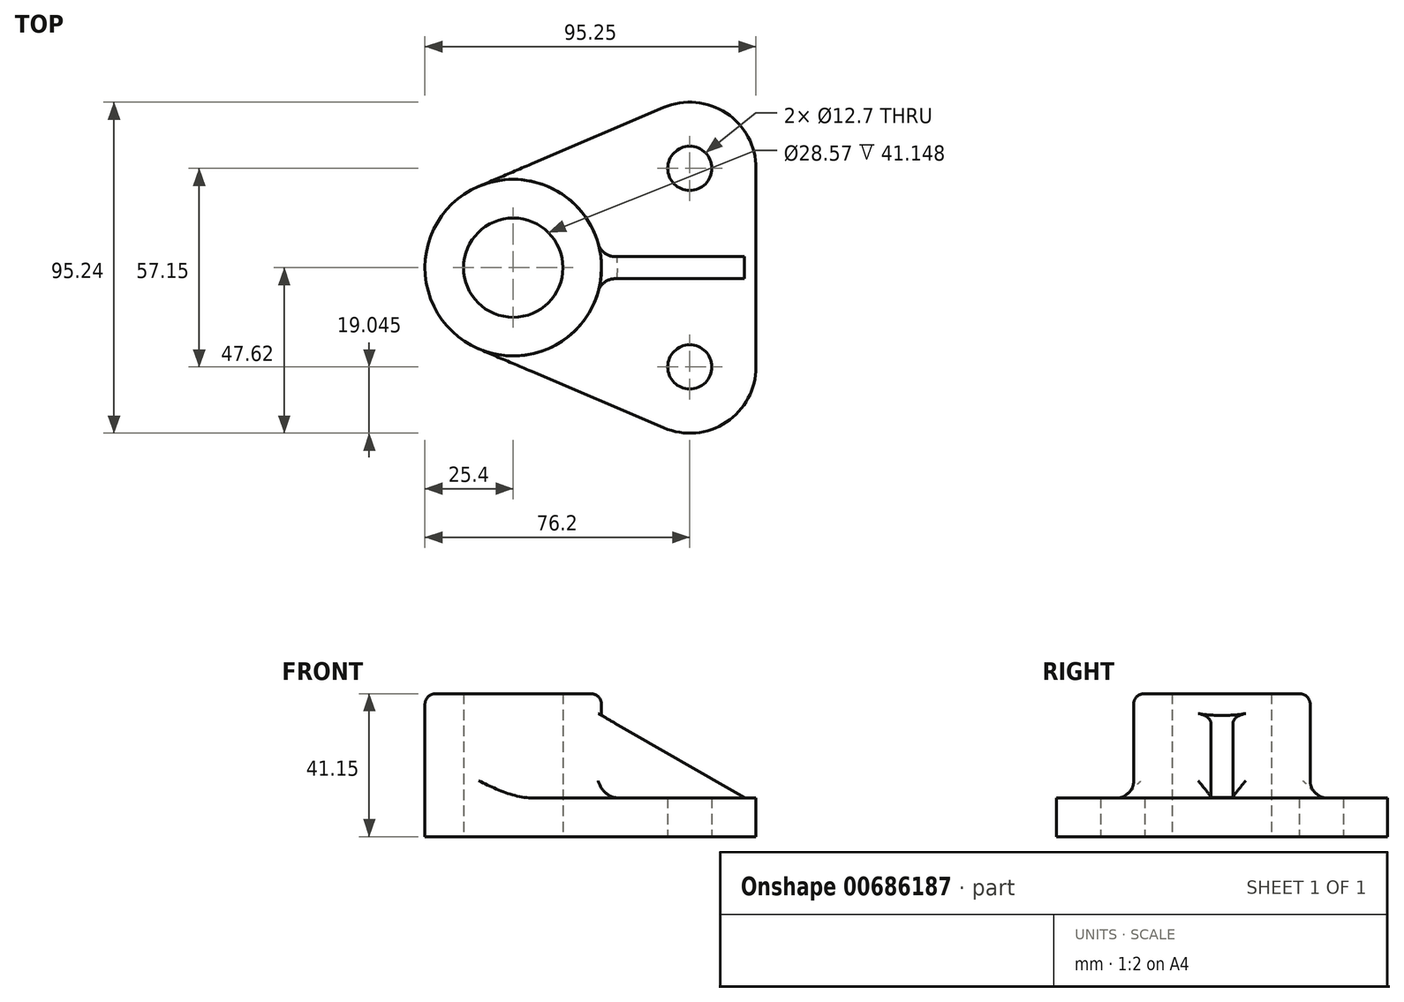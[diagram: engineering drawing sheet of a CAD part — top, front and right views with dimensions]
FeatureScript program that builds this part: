
annotation { "Feature Type Name" : "Feature", "Feature Type Description" : "" }
export const myFeature = defineFeature(function(context is Context, id is Id, definition is map)
    precondition{}
    {
        {
            var Q0;
            Q0=qCreatedBy(makeId("Top.planeOp"),FACE);
            var sketch = newSketch(context, id + "F0", { "sketchPlane" : qUnion([Q0])});
            skCircle(sketch, "E0", {"center": v(0, 0) * mm, "radius": 25.4 * mm});
            skCircle(sketch, "E1", {"center": v(0, 0) * mm, "radius": 14.29 * mm});
            skLineSegment(sketch, "E2", {"start": v(-34.33, 0) * mm, "end": v(50.8, 0) * mm, "construction": true});
            skCircle(sketch, "E3", {"center": v(50.8, 28.58) * mm, "radius": 6.35 * mm});
            skCircle(sketch, "E4", {"center": v(50.8, -28.58) * mm, "radius": 6.35 * mm});
            skArc(sketch, "E5", {"start": v(69.85, 28.58) * mm, "mid": v(61.3, 44.47) * mm, "end": v(43.33, 46.1) * mm});
            skArc(sketch, "E6", {"start": v(43.33, -46.1) * mm, "mid": v(61.3, -44.47) * mm, "end": v(69.85, -28.58) * mm});
            skLineSegment(sketch, "E7", {"start": v(-9.97, 23.36) * mm, "end": v(43.33, 46.1) * mm});
            skLineSegment(sketch, "E8", {"start": v(-9.97, -23.36) * mm, "end": v(43.33, -46.1) * mm});
            skLineSegment(sketch, "E9", {"start": v(69.85, 28.58) * mm, "end": v(69.85, -28.58) * mm});
            skPoint(sketch, "E10.right.end.orphan", {"position": v(-66.55, 3.17) * mm});
            skPoint(sketch, "E11.orphan", {"position": v(-66.55, -3.18) * mm});
            skPoint(sketch, "E10.left.end.orphan", {"position": v(66.55, 3.18) * mm});
            skPoint(sketch, "E10.left.start.orphan", {"position": v(66.55, -3.18) * mm});
            skSolve(sketch);
        }
        {
            var Q0;
            Q0=makeQuery(id+"F0.imprint","IMPRINT",FACE,{"disambiguationData":[TD([[makeQuery(id+"F0.imprint","IMPRINT",EDGE,{"derivedFrom":sQuery(id+"F0.wireOp",EDGE,"E1")}),-1.0]])]});
            extrude(context, id + "F1", {"entities" : qUnion([Q0]), "depth" : 41.15 * mm, "offsetDistance" : 25.4 * mm});
        }
        {
            var Q0;
            Q0=makeQuery(id+"F0.imprint","IMPRINT",FACE,{"disambiguationData":[TD([[makeQuery(id+"F0.imprint","IMPRINT",EDGE,{"derivedFrom":sQuery(id+"F0.wireOp",EDGE,"E3")}),-1.0]])]});
            extrude(context, id + "F2", {"entities" : qUnion([Q0]), "operationType" : NewBodyOperationType.ADD, "depth" : 11.18 * mm, "offsetDistance" : 25.4 * mm});
        }
        {
            var Q0;
            Q0=qCreatedBy(makeId("Front.planeOp"),FACE);
            var sketch = newSketch(context, id + "F3", { "sketchPlane" : qUnion([Q0])});
            skLineSegment(sketch, "E12", {"start": v(25.4, 11.18) * mm, "end": v(66.55, 11.25) * mm});
            skLineSegment(sketch, "E13", {"start": v(66.55, 11.25) * mm, "end": v(22.94, 36.32) * mm});
            skLineSegment(sketch, "E14.bottom", {"start": v(22.94, 36.32) * mm, "end": v(22.92, 36.32) * mm});
            skLineSegment(sketch, "E14.top", {"start": v(25.4, 11.18) * mm, "end": v(22.92, 11.18) * mm});
            skLineSegment(sketch, "E14.right", {"start": v(22.92, 36.32) * mm, "end": v(22.92, 11.18) * mm});
            skSolve(sketch);
        }
        {
            var Q0;
            Q0=makeQuery(id+"F3.imprint","IMPRINT",FACE,{"disambiguationData":[TD([[makeQuery(id+"F3.imprint","IMPRINT",EDGE,{"derivedFrom":sQuery(id+"F3.wireOp",EDGE,"E12")}),1.0]])]});
            extrude(context, id + "F4", {"entities" : qUnion([Q0]), "operationType" : NewBodyOperationType.ADD, "endBound" : BoundingType.SYMMETRIC, "depth" : 6.35 * mm, "offsetDistance" : 25.4 * mm});
        }
        {
            var Q0;
            Q0=makeQuery(id+"F1.opExtrude","CAP_EDGE",EDGE,{"disambiguationData":[OSD([sQuery(id+"F0.wireOp",EDGE,"E0")])],"isStart":false});
            fillet(context, id + "F5", {"entities" : qUnion([Q0]), "radius" : 3.05 * mm, "tangentPropagation" : true, "allowEdgeOverflow" : false});
        }
        {
            var Q0;
            Q0=makeQuery(id+"F4.boolean.opBoolean","INTERSECT",EDGE,{"derivedFrom":[makeQuery(id+"F1.opExtrude","SWEPT_FACE",FACE,{"disambiguationData":[OSD([sQuery(id+"F0.wireOp",EDGE,"E0")])]}),makeQuery(id+"F4.opExtrude","CAP_FACE",FACE,{"disambiguationData":[OSD([sQuery(id+"F3.wireOp",EDGE,"E12"),sQuery(id+"F3.wireOp",EDGE,"E13"),sQuery(id+"F3.wireOp",EDGE,"E14.bottom"),sQuery(id+"F3.wireOp",EDGE,"E14.top"),sQuery(id+"F3.wireOp",EDGE,"E14.right")])],"isStart":false})]});
            var Q1;
            Q1=makeQuery(id+"F4.boolean.opBoolean","INTERSECT",EDGE,{"derivedFrom":[makeQuery(id+"F1.opExtrude","SWEPT_FACE",FACE,{"disambiguationData":[OSD([sQuery(id+"F0.wireOp",EDGE,"E0")])]}),makeQuery(id+"F4.opExtrude","CAP_FACE",FACE,{"disambiguationData":[OSD([sQuery(id+"F3.wireOp",EDGE,"E12"),sQuery(id+"F3.wireOp",EDGE,"E13"),sQuery(id+"F3.wireOp",EDGE,"E14.bottom"),sQuery(id+"F3.wireOp",EDGE,"E14.top"),sQuery(id+"F3.wireOp",EDGE,"E14.right")])],"isStart":true})]});
            fillet(context, id + "F6", {"entities" : qUnion([Q0, Q1]), "radius" : 5.08 * mm, "tangentPropagation" : true, "allowEdgeOverflow" : false});
        }
        {
            var Q0;
            {var subQ0=sQuery(id+"F0.wireOp",EDGE,"E0");Q0=makeQuery(id+"F6.opFillet","BLEND_EDGE",EDGE,{"blendedFrom":[makeQuery(id+"F4.boolean.opBoolean","INTERSECT",EDGE,{"derivedFrom":[makeQuery(id+"F1.opExtrude","SWEPT_FACE",FACE,{"disambiguationData":[OSD([subQ0])]}),makeQuery(id+"F4.opExtrude","CAP_FACE",FACE,{"disambiguationData":[OSD([sQuery(id+"F3.wireOp",EDGE,"E12"),sQuery(id+"F3.wireOp",EDGE,"E13"),sQuery(id+"F3.wireOp",EDGE,"E14.bottom"),sQuery(id+"F3.wireOp",EDGE,"E14.top"),sQuery(id+"F3.wireOp",EDGE,"E14.right")])],"isStart":false})]}),makeQuery(id+"F2.opExtrude","CAP_FACE",FACE,{"disambiguationData":[OSD([subQ0,sQuery(id+"F0.wireOp",EDGE,"E3"),sQuery(id+"F0.wireOp",EDGE,"E4"),sQuery(id+"F0.wireOp",EDGE,"E5"),sQuery(id+"F0.wireOp",EDGE,"E6"),sQuery(id+"F0.wireOp",EDGE,"E7"),sQuery(id+"F0.wireOp",EDGE,"E8"),sQuery(id+"F0.wireOp",EDGE,"E9")])],"isStart":false})],"blendedInto":[makeQuery(id+"F2.opExtrude","CAP_FACE",FACE,{"disambiguationData":[OSD([subQ0,sQuery(id+"F0.wireOp",EDGE,"E3"),sQuery(id+"F0.wireOp",EDGE,"E4"),sQuery(id+"F0.wireOp",EDGE,"E5"),sQuery(id+"F0.wireOp",EDGE,"E6"),sQuery(id+"F0.wireOp",EDGE,"E7"),sQuery(id+"F0.wireOp",EDGE,"E8"),sQuery(id+"F0.wireOp",EDGE,"E9")])],"isStart":false})]});}
            fillet(context, id + "F7", {"entities" : qUnion([Q0]), "radius" : 4.9 * mm, "tangentPropagation" : true, "allowEdgeOverflow" : false});
        }
    });
